# Revit family: 54R
name_source: partatom
category: Lighting Fixtures
units: mm (PartAtom-declared; Revit-internal decimal feet)

## family parameters
Always vertical = Yes
Cut with Voids When Loaded = No
Host = Wall
Light Source = Yes
OmniClass Number = 23.80.70.11.14.17
OmniClass Title = Direct/Indirect
Part Type = Normal
Room Calculation Point = No
Round Connector Dimension = Use Diameter
Shared = No

## types (5) — shared parameters
Apparent Load = 4 VA
Assembly Code = D5020210
Color Filter = 16777215
Default Elevation = 0"
Description = Arcos Wall LED
Dimming Lamp Color Temperature Shift = <None>
Emit Shape Visible in Rendering = No
Emit from Rectangle Width = 2"
Fixture distribution = Asymmetric Indirect
Lamp = LED
Load Classification = Lighting
Manufacturer = LiteControl
Model = 54L W
Mounting = Wall-Mounted
Photometric Web File = generic
Power Factor = 1
Product Material = Paint -  Matte White
Reflector Finish = White Glass
Tilt Angle = -90.00°
URL = https://www.currentlighting.com
Watts = 4 W

## per-type parameters (varying)
| type | Emit from Rectangle Length | Length |
| 54L-W-02 | 22" | 24" |
| 54L-W-03 | 34" | 36" |
| 54L-W-04 | 46" | 48" |
| 54L-W-06 | 70" | 72" |
| 54L-W-08 | 94" | 96" |

## geometry (parser evidence)
native form markers: Blend x6, Sweep x3
no freeform markers — native parametric forms only
